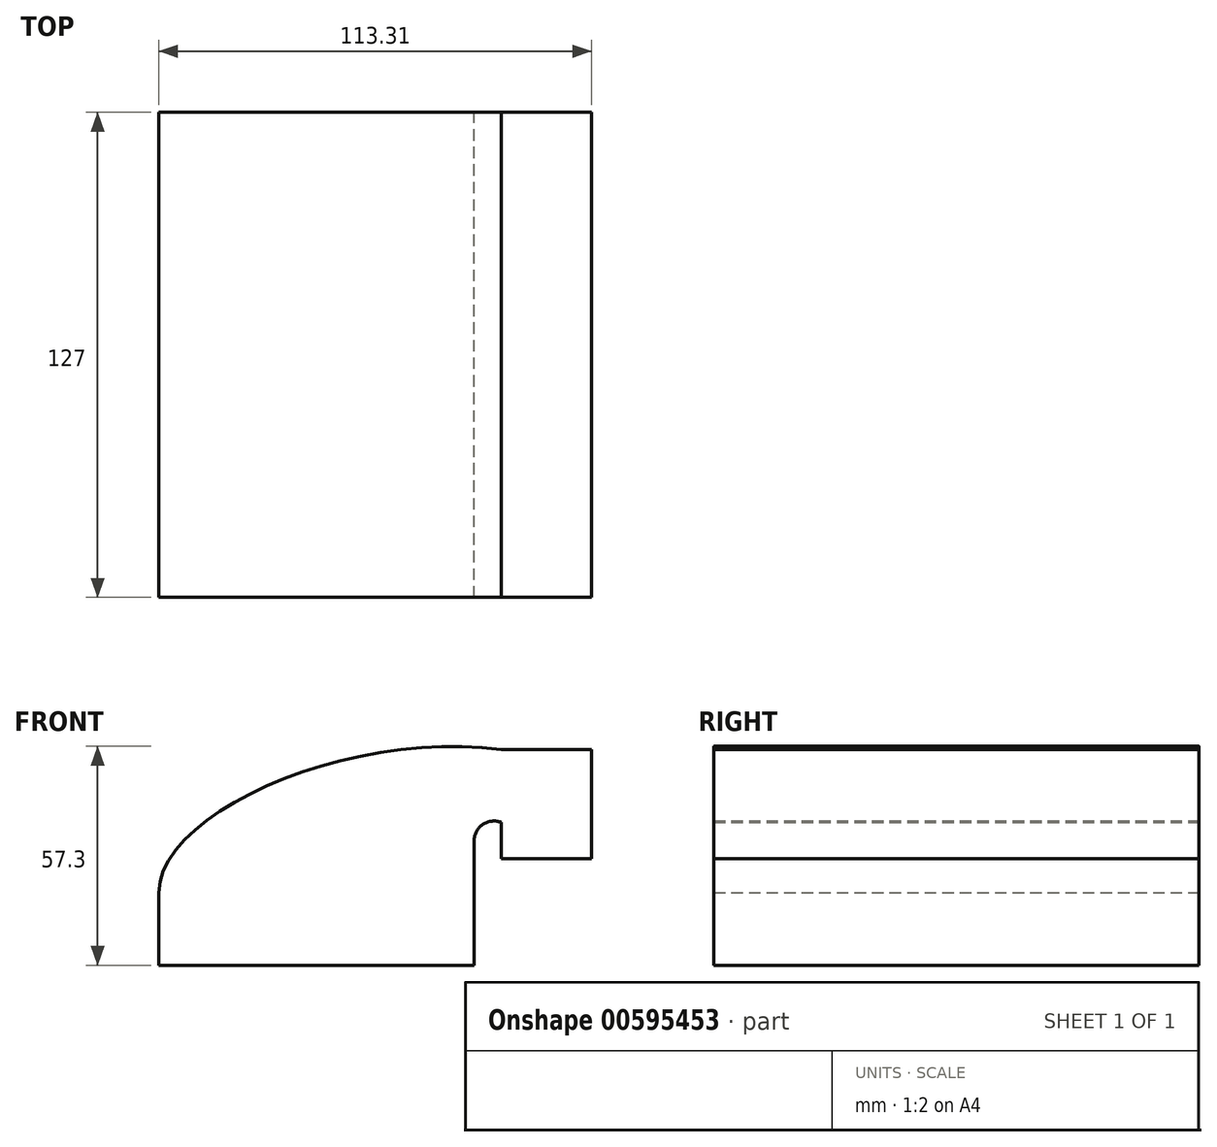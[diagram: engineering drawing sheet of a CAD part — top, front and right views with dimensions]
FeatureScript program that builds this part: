
annotation { "Feature Type Name" : "Feature", "Feature Type Description" : "" }
export const myFeature = defineFeature(function(context is Context, id is Id, definition is map)
    precondition{}
    {
        {
            var Q0;
            Q0=qCreatedBy(makeId("Front.planeOp"),FACE);
            var sketch = newSketch(context, id + "F0", { "sketchPlane" : qUnion([Q0])});
            skLineSegment(sketch, "E0.bottom", {"start": v(-41.28, 9.52) * mm, "end": v(41.28, 9.53) * mm});
            skLineSegment(sketch, "E0.top", {"start": v(-41.28, -9.53) * mm, "end": v(41.28, -9.53) * mm});
            skLineSegment(sketch, "E0.left", {"start": v(-41.28, 9.52) * mm, "end": v(-41.28, -9.53) * mm});
            skLineSegment(sketch, "E0.right", {"start": v(41.28, 9.53) * mm, "end": v(41.28, -9.52) * mm});
            skPoint(sketch, "E0.middle", {"position": v(0, 0) * mm});
            skLineSegment(sketch, "E1.bottom", {"start": v(48.43, 46.9) * mm, "end": v(72.03, 46.9) * mm});
            skLineSegment(sketch, "E1.top", {"start": v(48.43, 18.33) * mm, "end": v(72.03, 18.33) * mm});
            skLineSegment(sketch, "E1.left", {"start": v(48.43, 46.9) * mm, "end": v(48.43, 18.33) * mm});
            skLineSegment(sketch, "E1.right", {"start": v(72.03, 46.9) * mm, "end": v(72.03, 18.33) * mm});
            skPoint(sketch, "E1.middle", {"position": v(60.23, 32.62) * mm});
            skLineSegment(sketch, "E2", {"start": v(41.27, 9.53) * mm, "end": v(41.27, 23) * mm});
            skArc(sketch, "E3", {"start": v(41.28, 23) * mm, "mid": v(43.56, 27.33) * mm, "end": v(48.43, 27.87) * mm});
            skLineSegment(sketch, "E4", {"start": v(48.43, 27.87) * mm, "end": v(58.27, 27.87) * mm});
            skLineSegment(sketch, "E5.0", {"start": v(50.43, 43.93) * mm, "end": v(58.27, 43.93) * mm});
            skArc(sketch, "E5.1", {"start": v(25.21, 23) * mm, "mid": v(32.9, 39.39) * mm, "end": v(50.43, 43.93) * mm});
            skLineSegment(sketch, "E5.2", {"start": v(25.21, 9.53) * mm, "end": v(25.21, 23) * mm});
            skFitSpline(sketch, "E6", {"points": [v(-41.28, 9.52) * mm, v(48.43, 46.9) * mm], "startDerivative": vector(1.23, 64.67) * mm, "endDerivative": vector(115.97, -16.4) * mm});
            skSolve(sketch);
        }
        {
            var Q0;
            Q0 = qSketchRegion(id + "F0", true);
            extrude(context, id + "F1", {"entities" : qUnion([Q0]), "endBound" : BoundingType.SYMMETRIC, "depth" : 127 * mm, "offsetDistance" : 25.4 * mm});
        }
    });
